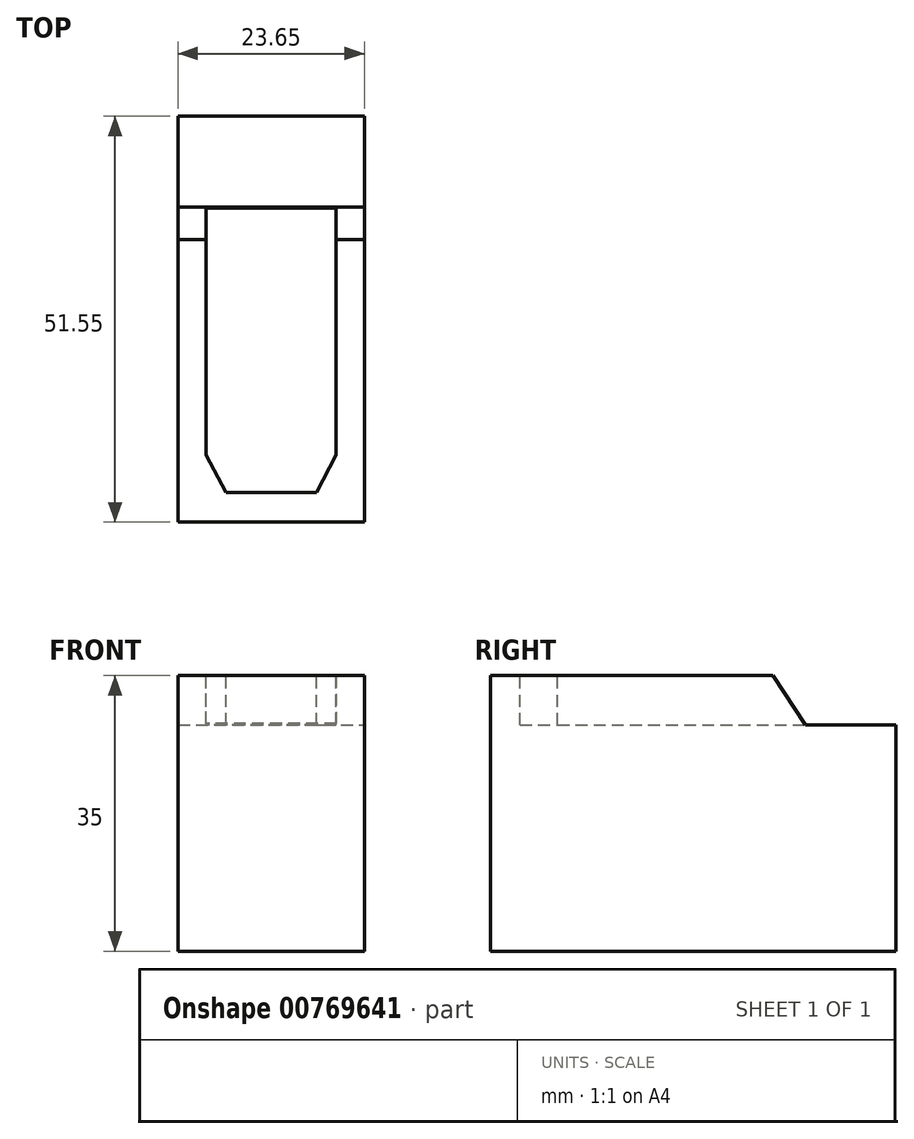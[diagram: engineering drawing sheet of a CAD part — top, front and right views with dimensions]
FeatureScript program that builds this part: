
annotation { "Feature Type Name" : "Feature", "Feature Type Description" : "" }
export const myFeature = defineFeature(function(context is Context, id is Id, definition is map)
    precondition{}
    {
        {
            var Q0;
            Q0=qCreatedBy(makeId("Top.planeOp"),FACE);
            var sketch = newSketch(context, id + "F0", { "sketchPlane" : qUnion([Q0])});
            skLineSegment(sketch, "E0", {"start": v(-11.06, 0) * mm, "end": v(-11.06, -51.55) * mm});
            skLineSegment(sketch, "E1", {"start": v(-11.06, -51.55) * mm, "end": v(12.59, -51.55) * mm});
            skLineSegment(sketch, "E2", {"start": v(12.59, -51.55) * mm, "end": v(12.59, 0) * mm});
            skLineSegment(sketch, "E3", {"start": v(-11.06, 0) * mm, "end": v(12.59, 0) * mm});
            skSolve(sketch);
        }
        {
            var Q0;
            Q0=qSketchRegion(id+"F0",true);
            extrude(context, id + "F1", {"entities" : qUnion([Q0]), "depth" : 35 * mm, "offsetDistance" : 25.4 * mm});
        }
        {
            var Q0;
            Q0=makeQuery(id+"F1.opExtrude","SWEPT_FACE",FACE,{"disambiguationData":[OSD([sQuery(id+"F0.wireOp",EDGE,"E2")])]});
            var sketch = newSketch(context, id + "F2", { "sketchPlane" : qUnion([Q0])});
            skLineSegment(sketch, "E4", {"start": v(0, 35) * mm, "end": v(0, 28.75) * mm});
            skLineSegment(sketch, "E5", {"start": v(-11.5, 28.75) * mm, "end": v(-15.66, 35) * mm});
            skLineSegment(sketch, "E6", {"start": v(-11.5, 28.75) * mm, "end": v(0, 28.75) * mm});
            skLineSegment(sketch, "E7", {"start": v(0, 35) * mm, "end": v(-15.66, 35) * mm});
            skSolve(sketch);
        }
        {
            var Q0;
            Q0=qSketchRegion(id+"F2",true);
            extrude(context, id + "F3", {"entities" : qUnion([Q0]), "operationType" : NewBodyOperationType.REMOVE, "endBound" : BoundingType.THROUGH_ALL, "oppositeDirection" : true, "depth" : 25.4 * mm, "offsetDistance" : 25.4 * mm});
        }
        {
            var Q0;
            Q0=makeQuery(id+"F1.opExtrude","CAP_FACE",FACE,{"disambiguationData":[OSD([sQuery(id+"F0.wireOp",EDGE,"E0"),sQuery(id+"F0.wireOp",EDGE,"E1"),sQuery(id+"F0.wireOp",EDGE,"E2"),sQuery(id+"F0.wireOp",EDGE,"E3")])],"isStart":false});
            var sketch = newSketch(context, id + "F4", { "sketchPlane" : qUnion([Q0])});
            skLineSegment(sketch, "E8", {"start": v(0.76, -47.76) * mm, "end": v(6.51, -47.76) * mm});
            skLineSegment(sketch, "E9.MirrorCS", {"start": v(0.76, -47.76) * mm, "end": v(-4.99, -47.76) * mm});
            skLineSegment(sketch, "E10", {"start": v(0.76, -15.66) * mm, "end": v(9.01, -15.66) * mm});
            skLineSegment(sketch, "E11", {"start": v(6.51, -47.76) * mm, "end": v(9.01, -43) * mm});
            skLineSegment(sketch, "E12", {"start": v(9.01, -43) * mm, "end": v(9.01, -15.66) * mm});
            skLineSegment(sketch, "E13.MirrorCS", {"start": v(-7.49, -43) * mm, "end": v(-7.49, -15.66) * mm});
            skLineSegment(sketch, "E14.MirrorCS", {"start": v(0.76, -15.66) * mm, "end": v(-7.49, -15.66) * mm});
            skLineSegment(sketch, "E15.MirrorCS", {"start": v(-4.99, -47.76) * mm, "end": v(-7.49, -43) * mm});
            skSolve(sketch);
        }
        {
            var Q0;
            Q0=qSketchRegion(id+"F4",true);
            extrude(context, id + "F5", {"entities" : qUnion([Q0]), "operationType" : NewBodyOperationType.REMOVE, "oppositeDirection" : true, "depth" : 6.25 * mm, "offsetDistance" : 25.4 * mm});
        }
        {
            var Q0;
            Q0=makeQuery(id+"F1.opExtrude","CAP_FACE",FACE,{"disambiguationData":[OSD([sQuery(id+"F0.wireOp",EDGE,"E0"),sQuery(id+"F0.wireOp",EDGE,"E1"),sQuery(id+"F0.wireOp",EDGE,"E2"),sQuery(id+"F0.wireOp",EDGE,"E3")])],"isStart":false});
            var sketch = newSketch(context, id + "F6", { "sketchPlane" : qUnion([Q0])});
            skLineSegment(sketch, "E16", {"start": v(-7.49, -15.66) * mm, "end": v(9.01, -15.66) * mm});
            skLineSegment(sketch, "E17", {"start": v(9.01, -15.66) * mm, "end": v(9.01, -11.62) * mm});
            skLineSegment(sketch, "E18", {"start": v(9.01, -11.62) * mm, "end": v(-7.49, -11.62) * mm});
            skLineSegment(sketch, "E19", {"start": v(-7.49, -11.62) * mm, "end": v(-7.49, -15.66) * mm});
            skSolve(sketch);
        }
        {
            var Q0;
            Q0=qSketchRegion(id+"F6",true);
            extrude(context, id + "F7", {"entities" : qUnion([Q0]), "operationType" : NewBodyOperationType.REMOVE, "oppositeDirection" : true, "depth" : 6.25 * mm, "offsetDistance" : 25.4 * mm});
        }
    });
